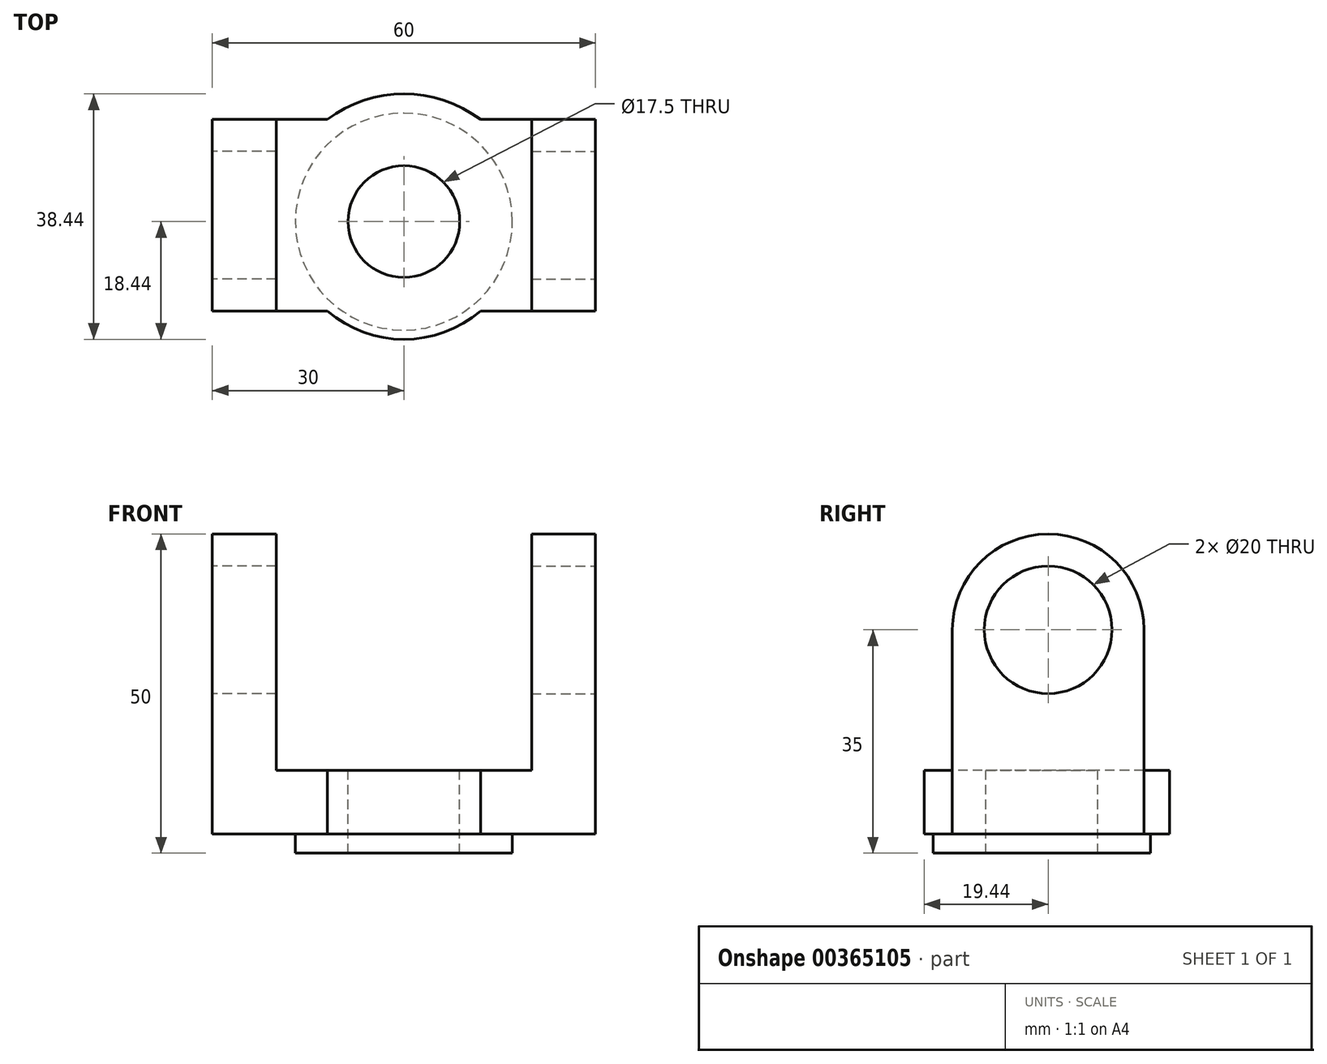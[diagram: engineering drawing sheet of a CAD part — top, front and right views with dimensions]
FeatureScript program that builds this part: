
annotation { "Feature Type Name" : "Feature", "Feature Type Description" : "" }
export const myFeature = defineFeature(function(context is Context, id is Id, definition is map)
    precondition{}
    {
        {
            var Q0;
            Q0=qCreatedBy(makeId("Top.planeOp"),FACE);
            var sketch = newSketch(context, id + "F0", { "sketchPlane" : qUnion([Q0])});
            skCircle(sketch, "E0", {"center": v(0, 0) * mm, "radius": 17 * mm});
            skSolve(sketch);
        }
        {
            var Q0;
            Q0 = qSketchRegion(id + "F0", true);
            extrude(context, id + "F1", {"entities" : qUnion([Q0]), "depth" : 3 * mm});
        }
        {
            var Q0;
            Q0=makeQuery(id+"F1.opExtrude","CAP_FACE",FACE,{"disambiguationData":[OSD([sQuery(id+"F0.wireOp",EDGE,"E0")])],"isStart":false});
            var sketch = newSketch(context, id + "F2", { "sketchPlane" : qUnion([Q0])});
            skLineSegment(sketch, "E1.bottom", {"start": v(-30, 16) * mm, "end": v(30, 16) * mm});
            skLineSegment(sketch, "E1.top", {"start": v(-30, -14) * mm, "end": v(30, -14) * mm});
            skLineSegment(sketch, "E1.left", {"start": v(-30, 16) * mm, "end": v(-30, -14) * mm});
            skLineSegment(sketch, "E1.right", {"start": v(30, 16) * mm, "end": v(30, -14) * mm});
            skArc(sketch, "E2", {"start": v(12, 16) * mm, "mid": v(0, 20) * mm, "end": v(-12, 16) * mm});
            skArc(sketch, "E3", {"start": v(-12, -14) * mm, "mid": v(0, -18.44) * mm, "end": v(12, -14) * mm});
            skSolve(sketch);
        }
        {
            var Q0;
            Q0 = qSketchRegion(id + "F2", true);
            extrude(context, id + "F3", {"entities" : qUnion([Q0]), "operationType" : NewBodyOperationType.ADD, "depth" : 10 * mm});
        }
        {
            var Q0;
            Q0=makeQuery(id+"F3.opExtrude","SWEPT_FACE",FACE,{"disambiguationData":[OSD([sQuery(id+"F2.wireOp",EDGE,"E1.right")])]});
            var sketch = newSketch(context, id + "F4", { "sketchPlane" : qUnion([Q0])});
            skLineSegment(sketch, "E4", {"start": v(-14, 13) * mm, "end": v(16, 13) * mm});
            skLineSegment(sketch, "E5", {"start": v(16, 13) * mm, "end": v(16, 35) * mm});
            skLineSegment(sketch, "E6", {"start": v(-14, 13) * mm, "end": v(-14, 35) * mm});
            skArc(sketch, "E7", {"start": v(16, 35) * mm, "mid": v(1, 50) * mm, "end": v(-14, 35) * mm});
            skCircle(sketch, "E8", {"center": v(1, 35) * mm, "radius": 10 * mm});
            skSolve(sketch);
        }
        {
            var Q0;
            Q0=makeQuery(id+"F4.imprint","IMPRINT",FACE,{"disambiguationData":[TD([[makeQuery(id+"F4.imprint","IMPRINT",EDGE,{"derivedFrom":sQuery(id+"F4.wireOp",EDGE,"E4")}),-1.0]])]});
            extrude(context, id + "F5", {"entities" : qUnion([Q0]), "operationType" : NewBodyOperationType.ADD, "oppositeDirection" : true, "depth" : 10 * mm});
        }
        {
            var Q0;
            Q0=makeQuery(id+"F3.opExtrude","SWEPT_FACE",FACE,{"disambiguationData":[OSD([sQuery(id+"F2.wireOp",EDGE,"E1.left")])]});
            var sketch = newSketch(context, id + "F6", { "sketchPlane" : qUnion([Q0])});
            skLineSegment(sketch, "E9", {"start": v(-16, 13) * mm, "end": v(14, 13) * mm});
            skLineSegment(sketch, "E10", {"start": v(14, 13) * mm, "end": v(14, 35) * mm});
            skLineSegment(sketch, "E11", {"start": v(-16, 13) * mm, "end": v(-16, 35) * mm});
            skArc(sketch, "E12", {"start": v(14, 35) * mm, "mid": v(-1, 50) * mm, "end": v(-16, 35) * mm});
            skCircle(sketch, "E13", {"center": v(-1, 35) * mm, "radius": 10 * mm});
            skSolve(sketch);
        }
        {
            var Q0;
            Q0=makeQuery(id+"F6.imprint","IMPRINT",FACE,{"disambiguationData":[TD([[makeQuery(id+"F6.imprint","IMPRINT",EDGE,{"derivedFrom":sQuery(id+"F6.wireOp",EDGE,"E9")}),1.0]])]});
            extrude(context, id + "F7", {"entities" : qUnion([Q0]), "operationType" : NewBodyOperationType.ADD, "oppositeDirection" : true, "depth" : 10 * mm});
        }
        {
            var Q0;
            Q0=makeQuery(id+"F3.opExtrude","CAP_FACE",FACE,{"disambiguationData":[OSD([sQuery(id+"F2.wireOp",EDGE,"E1.bottom"),sQuery(id+"F2.wireOp",EDGE,"E1.top"),sQuery(id+"F2.wireOp",EDGE,"E1.left"),sQuery(id+"F2.wireOp",EDGE,"E1.right"),sQuery(id+"F2.wireOp",EDGE,"E2"),sQuery(id+"F2.wireOp",EDGE,"E3")])],"isStart":false});
            var sketch = newSketch(context, id + "F8", { "sketchPlane" : qUnion([Q0])});
            skCircle(sketch, "E14", {"center": v(0, 0) * mm, "radius": 8.75 * mm});
            skSolve(sketch);
        }
        {
            var Q0;
            Q0=makeQuery(id+"F8.imprint","IMPRINT",FACE,{"disambiguationData":[TD([[makeQuery(id+"F8.imprint","IMPRINT",EDGE,{"derivedFrom":sQuery(id+"F8.wireOp",EDGE,"E14")}),1.0]])]});
            var Q1;
            Q1=sQuery(id+"F8.wireOp",EDGE,"E14");
            extrude(context, id + "F9", {"entities" : qUnion([Q0]), "operationType" : NewBodyOperationType.REMOVE, "surfaceEntities" : qUnion([Q1]), "endBound" : BoundingType.THROUGH_ALL, "oppositeDirection" : true, "depth" : 25 * mm});
        }
    });
